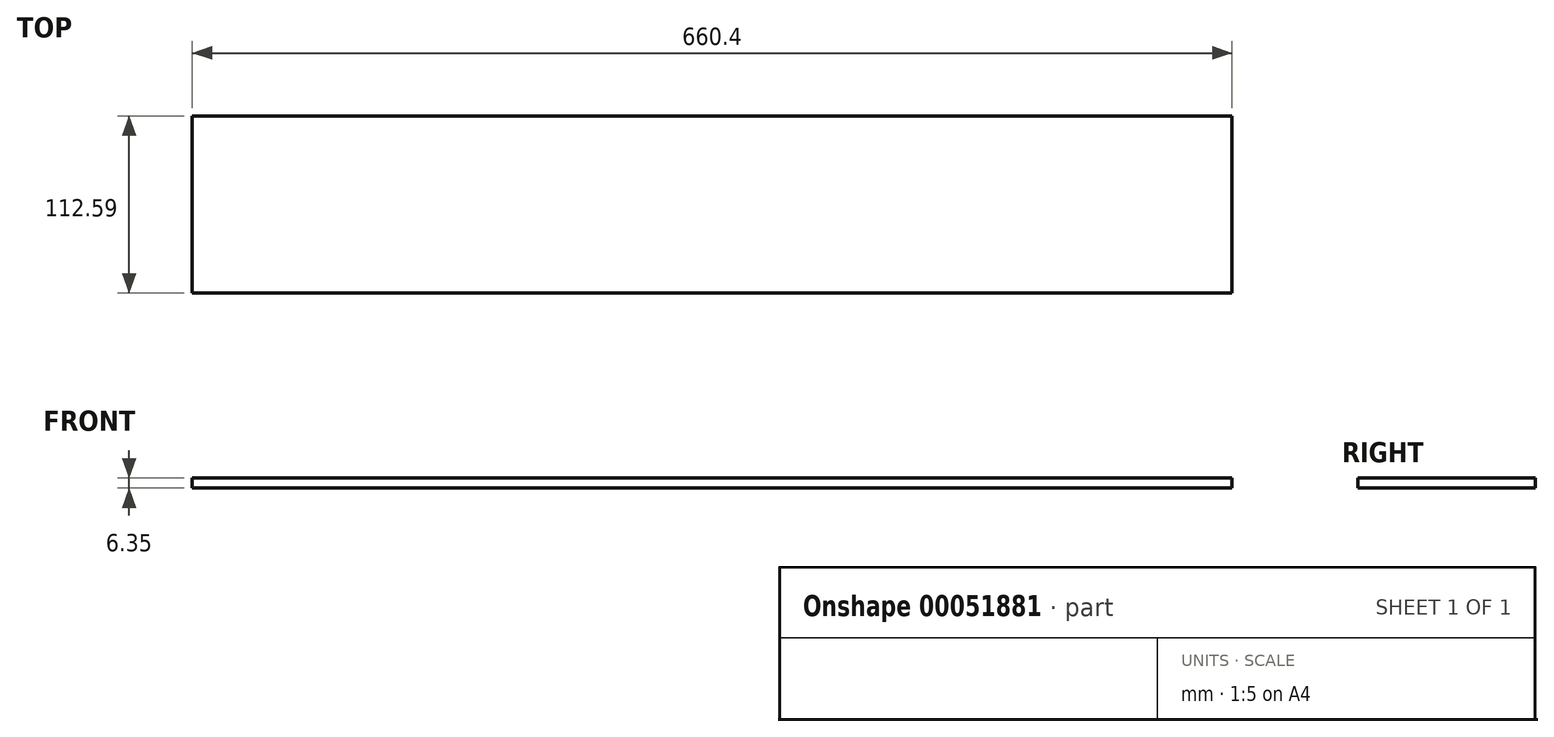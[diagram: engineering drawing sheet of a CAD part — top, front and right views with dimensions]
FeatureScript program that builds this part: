
annotation { "Feature Type Name" : "Feature", "Feature Type Description" : "" }
export const myFeature = defineFeature(function(context is Context, id is Id, definition is map)
    precondition{}
    {
        {
            var Q0;
            Q0=qCreatedBy(makeId("Top.planeOp"),FACE);
            var sketch = newSketch(context, id + "F0", { "sketchPlane" : qUnion([Q0])});
            skLineSegment(sketch, "E0.bottom", {"start": v(-330.2, 61.79) * mm, "end": v(330.2, 61.79) * mm});
            skLineSegment(sketch, "E0.top", {"start": v(-330.2, -50.8) * mm, "end": v(330.2, -50.8) * mm});
            skLineSegment(sketch, "E0.left", {"start": v(-330.2, 61.79) * mm, "end": v(-330.2, -50.8) * mm});
            skLineSegment(sketch, "E0.right", {"start": v(330.2, 61.79) * mm, "end": v(330.2, -50.8) * mm});
            skSolve(sketch);
        }
        {
            var Q0;
            Q0 = qSketchRegion(id + "F0", true);
            extrude(context, id + "F1", {"entities" : qUnion([Q0]), "depth" : 6.35 * mm});
        }
    });
